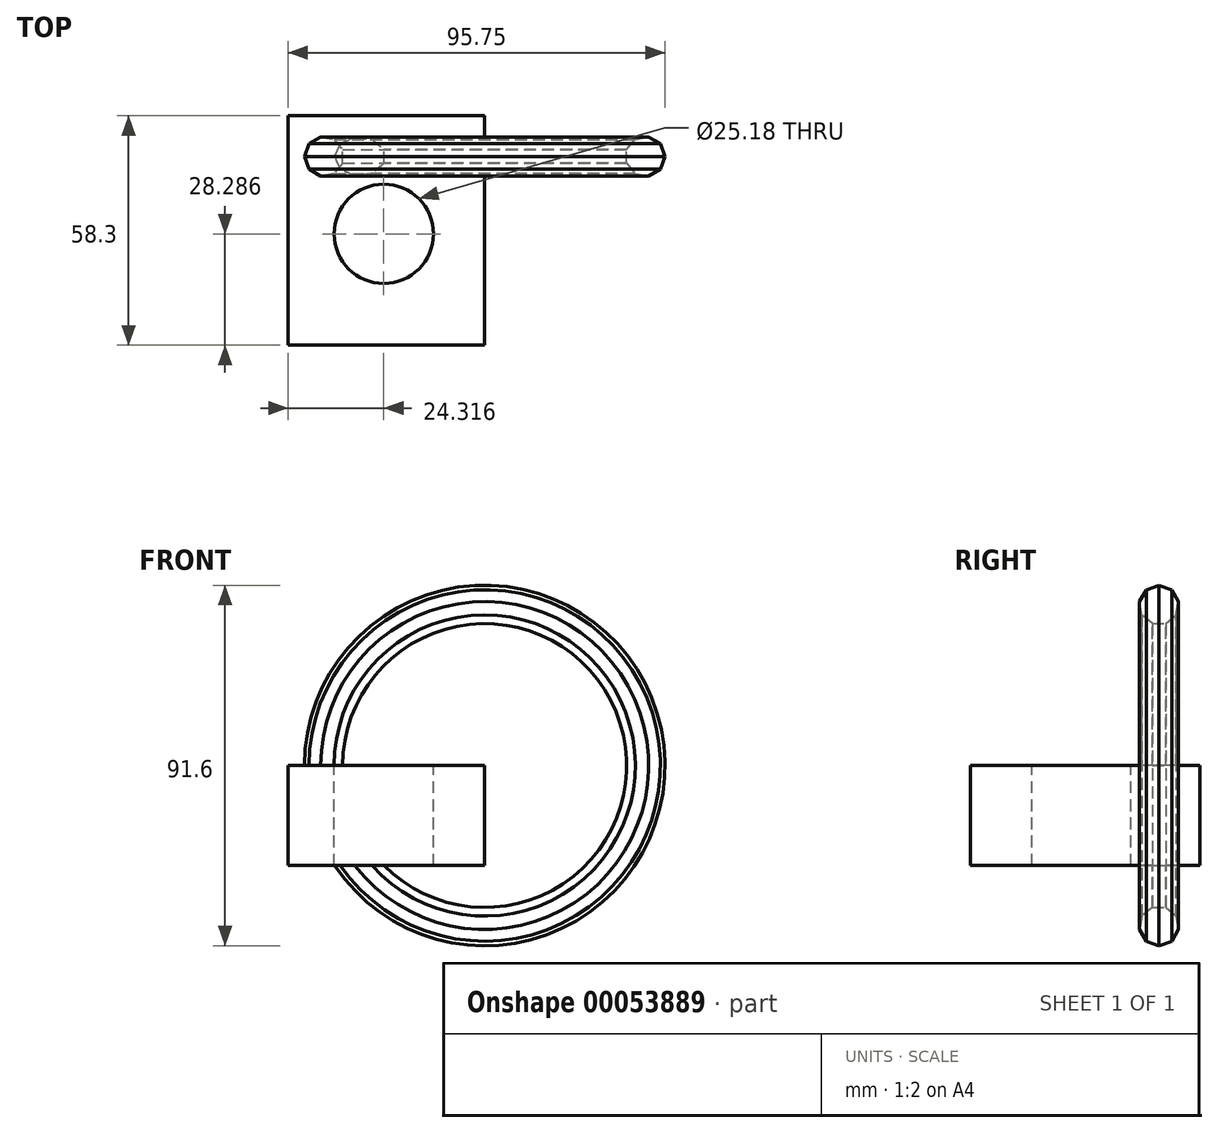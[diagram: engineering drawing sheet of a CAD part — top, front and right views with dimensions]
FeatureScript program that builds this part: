
annotation { "Feature Type Name" : "Feature", "Feature Type Description" : "" }
export const myFeature = defineFeature(function(context is Context, id is Id, definition is map)
    precondition{}
    {
        {
            var Q0;
            Q0=qCreatedBy(makeId("Top.planeOp"),FACE);
            var sketch = newSketch(context, id + "F0", { "sketchPlane" : qUnion([Q0])});
            skLineSegment(sketch, "E0.bottom", {"start": v(-127.34, 46.92) * mm, "end": v(-77.38, 46.92) * mm});
            skLineSegment(sketch, "E0.top", {"start": v(-127.34, -11.38) * mm, "end": v(-77.38, -11.38) * mm});
            skLineSegment(sketch, "E0.left", {"start": v(-127.34, 46.92) * mm, "end": v(-127.34, -11.38) * mm});
            skLineSegment(sketch, "E0.right", {"start": v(-77.38, 46.92) * mm, "end": v(-77.38, -11.38) * mm});
            skSolve(sketch);
        }
        {
            var Q0;
            Q0 = qSketchRegion(id + "F0", true);
            extrude(context, id + "F1", {"entities" : qUnion([Q0]), "endBound" : BoundingType.SYMMETRIC, "depth" : 25.4 * mm});
        }
        {
            var Q0;
            Q0=makeQuery(id+"F1.opExtrude","CAP_FACE",FACE,{"disambiguationData":[OSD([sQuery(id+"F0.wireOp",EDGE,"E0.bottom"),sQuery(id+"F0.wireOp",EDGE,"E0.top"),sQuery(id+"F0.wireOp",EDGE,"E0.left"),sQuery(id+"F0.wireOp",EDGE,"E0.right")])],"isStart":false});
            var sketch = newSketch(context, id + "F2", { "sketchPlane" : qUnion([Q0])});
            skCircle(sketch, "E1", {"center": v(-103.02, 16.9) * mm, "radius": 12.59 * mm});
            skSolve(sketch);
        }
        {
            var Q0;
            Q0 = qSketchRegion(id + "F2", true);
            extrude(context, id + "F3", {"entities" : qUnion([Q0]), "operationType" : NewBodyOperationType.REMOVE, "endBound" : BoundingType.THROUGH_ALL, "oppositeDirection" : true, "depth" : 25.4 * mm});
        }
        {
            var Q0;
            Q0=makeQuery(id+"F1.opExtrude","CAP_FACE",FACE,{"disambiguationData":[OSD([sQuery(id+"F0.wireOp",EDGE,"E0.bottom"),sQuery(id+"F0.wireOp",EDGE,"E0.top"),sQuery(id+"F0.wireOp",EDGE,"E0.left"),sQuery(id+"F0.wireOp",EDGE,"E0.right")])],"isStart":false});
            var sketch = newSketch(context, id + "F4", { "sketchPlane" : qUnion([Q0])});
            skCircle(sketch, "E2.cCircle", {"center": v(-118.16, 36.56) * mm, "radius": 4.72 * mm, "construction": true});
            skLineSegment(sketch, "E2.0", {"start": v(-113.44, 38.28) * mm, "end": v(-113.44, 34.85) * mm});
            skLineSegment(sketch, "E2.1", {"start": v(-113.44, 34.85) * mm, "end": v(-115.65, 32.22) * mm});
            skLineSegment(sketch, "E2.2", {"start": v(-115.65, 32.22) * mm, "end": v(-119.03, 31.62) * mm});
            skLineSegment(sketch, "E2.3", {"start": v(-119.03, 31.62) * mm, "end": v(-122, 33.34) * mm});
            skLineSegment(sketch, "E2.4", {"start": v(-122, 33.34) * mm, "end": v(-123.18, 36.56) * mm});
            skLineSegment(sketch, "E2.5", {"start": v(-123.18, 36.56) * mm, "end": v(-122, 39.8) * mm});
            skLineSegment(sketch, "E2.6", {"start": v(-122, 39.8) * mm, "end": v(-119.03, 41.5) * mm});
            skLineSegment(sketch, "E2.7", {"start": v(-119.03, 41.5) * mm, "end": v(-115.65, 40.91) * mm});
            skLineSegment(sketch, "E2.8", {"start": v(-115.65, 40.91) * mm, "end": v(-113.44, 38.28) * mm});
            skPoint(sketch, "E2.0.midPoint", {"position": v(-113.44, 36.56) * mm});
            skSolve(sketch);
        }
        {
            var Q0;
            Q0 = qSketchRegion(id + "F4", true);
            var Q1;
            Q1=makeQuery(id+"F1.opExtrude","CAP_EDGE",EDGE,{"disambiguationData":[OSD([sQuery(id+"F0.wireOp",EDGE,"E0.right")])],"isStart":false});
            revolve(context, id + "F5", {"operationType" : NewBodyOperationType.ADD, "entities" : qUnion([Q0]), "axis" : qUnion([Q1]), "revolveType" : RevolveType.FULL});
        }
    });
